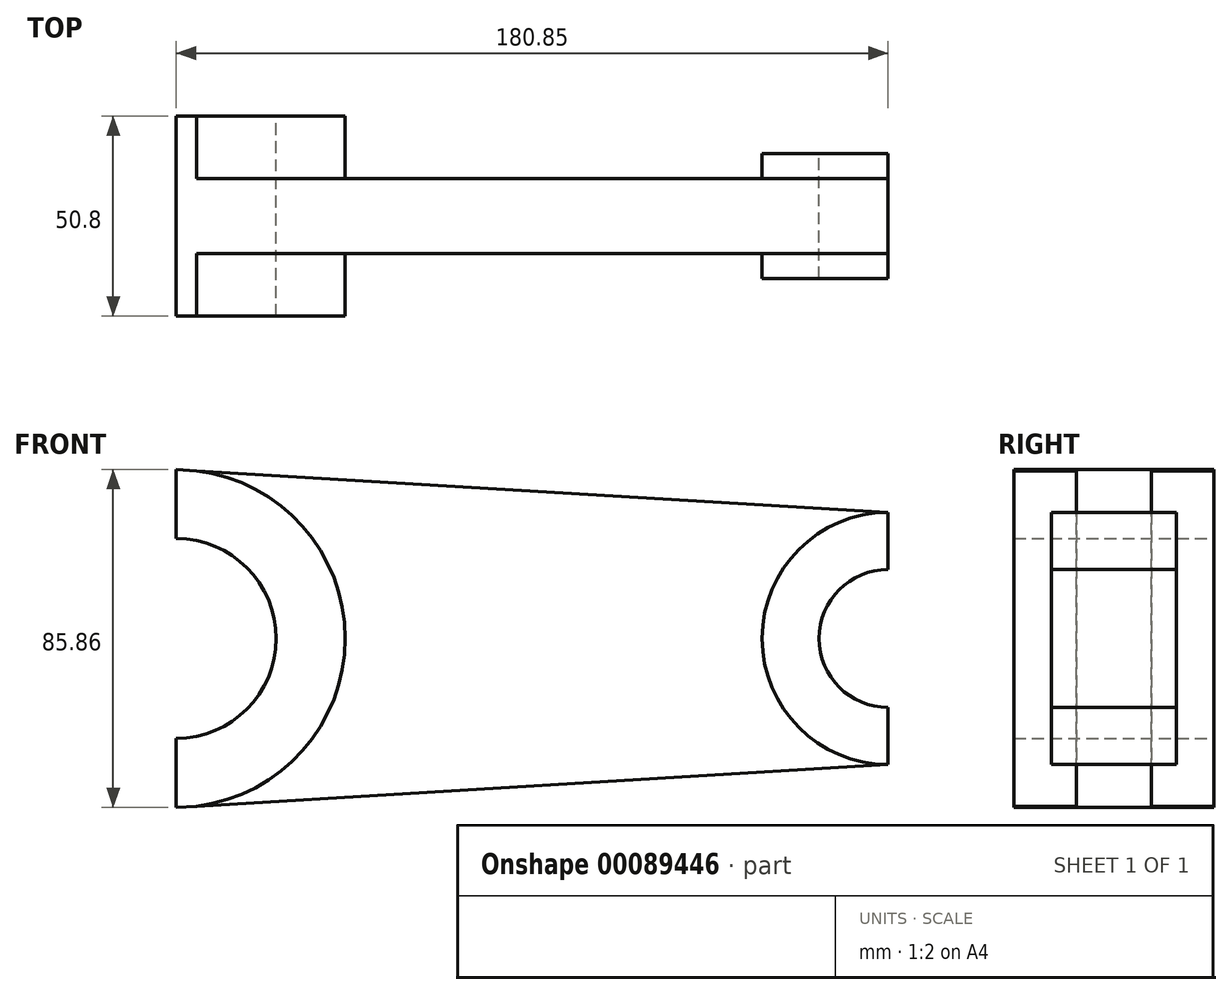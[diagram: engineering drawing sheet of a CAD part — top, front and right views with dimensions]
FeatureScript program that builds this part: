
annotation { "Feature Type Name" : "Feature", "Feature Type Description" : "" }
export const myFeature = defineFeature(function(context is Context, id is Id, definition is map)
    precondition{}
    {
        {
            var Q0;
            Q0=qCreatedBy(makeId("Front.planeOp"),FACE);
            var sketch = newSketch(context, id + "F0", { "sketchPlane" : qUnion([Q0])});
            skCircle(sketch, "E0", {"center": v(0, 0) * mm, "radius": 42.93 * mm});
            skLineSegment(sketch, "E1", {"start": v(0, 0) * mm, "end": v(180.85, 0) * mm});
            skCircle(sketch, "E2", {"center": v(180.85, 0) * mm, "radius": 32 * mm});
            skLineSegment(sketch, "E3", {"start": v(0, 0) * mm, "end": v(0, 42.93) * mm});
            skLineSegment(sketch, "E4", {"start": v(0, 42.93) * mm, "end": v(0, -42.93) * mm});
            skLineSegment(sketch, "E5", {"start": v(0, -42.93) * mm, "end": v(0, 0) * mm});
            skLineSegment(sketch, "E6", {"start": v(180.85, 0) * mm, "end": v(180.85, 32) * mm});
            skLineSegment(sketch, "E7", {"start": v(180.85, 32) * mm, "end": v(180.85, -32) * mm});
            skLineSegment(sketch, "E8", {"start": v(180.85, -32) * mm, "end": v(0, -42.93) * mm});
            skLineSegment(sketch, "E9", {"start": v(0, 42.93) * mm, "end": v(180.85, 32) * mm});
            skCircle(sketch, "E10", {"center": v(0, 0) * mm, "radius": 25.4 * mm});
            skCircle(sketch, "E11", {"center": v(180.85, 0) * mm, "radius": 17.53 * mm});
            skSolve(sketch);
        }
        {
            var Q0;
            {var subQ0=sQuery(id+"F0.wireOp",EDGE,"E8");var subQ1=sQuery(id+"F0.wireOp",EDGE,"E0");var subQ2=makeQuery(id+"F0.imprint","INTERSECT",VERTEX,{"derivedFrom":[subQ1,subQ0]});Q0=makeQuery(id+"F0.imprint","IMPRINT",FACE,{"disambiguationData":[TD([[makeQuery(id+"F0.imprint","IMPRINT",EDGE,{"disambiguationData":[TD([[subQ2,-1.0]])],"derivedFrom":subQ1}),-1.0]])]});}
            var Q1;
            {var subQ0=sQuery(id+"F0.wireOp",EDGE,"E9");var subQ1=sQuery(id+"F0.wireOp",EDGE,"E0");var subQ2=makeQuery(id+"F0.imprint","INTERSECT",VERTEX,{"derivedFrom":[subQ1,subQ0]});Q1=makeQuery(id+"F0.imprint","IMPRINT",FACE,{"disambiguationData":[TD([[makeQuery(id+"F0.imprint","IMPRINT",EDGE,{"disambiguationData":[TD([[subQ2,1.0]])],"derivedFrom":subQ1}),-1.0]])]});}
            extrude(context, id + "F1", {"entities" : qUnion([Q0, Q1]), "depth" : 19.05 * mm});
        }
        {
            var Q0;
            {var subQ0=sQuery(id+"F0.wireOp",EDGE,"E4");var subQ5=sQuery(id+"F0.wireOp",EDGE,"E10");var subQ6=makeQuery(id+"F0.imprint","INTERSECT",VERTEX,{"derivedFrom":[subQ0,subQ5]});Q0=makeQuery(id+"F0.imprint","IMPRINT",FACE,{"disambiguationData":[TD([[makeQuery(id+"F0.imprint","IMPRINT",EDGE,{"disambiguationData":[TD([[subQ6,-1.0]])],"derivedFrom":subQ5}),-1.0]])]});}
            var Q1;
            {var subQ0=sQuery(id+"F0.wireOp",EDGE,"E9");var subQ2=sQuery(id+"F0.wireOp",EDGE,"E0");var subQ9=makeQuery(id+"F0.imprint","INTERSECT",VERTEX,{"derivedFrom":[subQ2,subQ0]});Q1=makeQuery(id+"F0.imprint","IMPRINT",FACE,{"disambiguationData":[TD([[makeQuery(id+"F0.imprint","IMPRINT",EDGE,{"disambiguationData":[TD([[subQ9,1.0]])],"derivedFrom":subQ2}),1.0]])]});}
            var Q2;
            {var subQ0=sQuery(id+"F0.wireOp",EDGE,"E8");var subQ2=sQuery(id+"F0.wireOp",EDGE,"E0");var subQ6=makeQuery(id+"F0.imprint","INTERSECT",VERTEX,{"derivedFrom":[subQ2,subQ0]});Q2=makeQuery(id+"F0.imprint","IMPRINT",FACE,{"disambiguationData":[TD([[makeQuery(id+"F0.imprint","IMPRINT",EDGE,{"disambiguationData":[TD([[subQ6,-1.0]])],"derivedFrom":subQ2}),1.0]])]});}
            extrude(context, id + "F2", {"entities" : qUnion([Q0, Q1, Q2]), "operationType" : NewBodyOperationType.ADD, "depth" : 34.92 * mm});
        }
        {
            var Q0;
            {var subQ0=sQuery(id+"F0.wireOp",EDGE,"E2");var subQ1=sQuery(id+"F0.wireOp",EDGE,"E1");var subQ2=makeQuery(id+"F0.imprint","INTERSECT",VERTEX,{"derivedFrom":[subQ1,subQ0]});Q0=makeQuery(id+"F0.imprint","IMPRINT",FACE,{"disambiguationData":[TD([[makeQuery(id+"F0.imprint","IMPRINT",EDGE,{"disambiguationData":[TD([[subQ2,-1.0]])],"derivedFrom":subQ1}),1.0]])]});}
            var Q1;
            {var subQ0=sQuery(id+"F0.wireOp",EDGE,"E2");var subQ1=sQuery(id+"F0.wireOp",EDGE,"E1");var subQ2=makeQuery(id+"F0.imprint","INTERSECT",VERTEX,{"derivedFrom":[subQ1,subQ0]});Q1=makeQuery(id+"F0.imprint","IMPRINT",FACE,{"disambiguationData":[TD([[makeQuery(id+"F0.imprint","IMPRINT",EDGE,{"disambiguationData":[TD([[subQ2,-1.0]])],"derivedFrom":subQ1}),-1.0]])]});}
            var Q2;
            {var subQ0=sQuery(id+"F0.wireOp",EDGE,"E7");var subQ4=sQuery(id+"F0.wireOp",EDGE,"E11");var subQ5=makeQuery(id+"F0.imprint","INTERSECT",VERTEX,{"disambiguationData":[OD(0.0)],"derivedFrom":[subQ0,subQ4]});Q2=makeQuery(id+"F0.imprint","IMPRINT",FACE,{"disambiguationData":[TD([[makeQuery(id+"F0.imprint","IMPRINT",EDGE,{"disambiguationData":[TD([[subQ5,1.0]])],"derivedFrom":subQ4}),-1.0]])]});}
            var Q3;
            {var subQ0=sQuery(id+"F0.wireOp",EDGE,"E7");var subQ4=sQuery(id+"F0.wireOp",EDGE,"E11");var subQ5=makeQuery(id+"F0.imprint","INTERSECT",VERTEX,{"disambiguationData":[OD(0.0)],"derivedFrom":[subQ0,subQ4]});Q3=makeQuery(id+"F0.imprint","IMPRINT",FACE,{"disambiguationData":[TD([[makeQuery(id+"F0.imprint","IMPRINT",EDGE,{"disambiguationData":[TD([[subQ5,1.0]])],"derivedFrom":subQ4}),-1.0]])]});}
            extrude(context, id + "F3", {"entities" : qUnion([Q0, Q1, Q2, Q3]), "operationType" : NewBodyOperationType.ADD, "depth" : 25.4 * mm});
        }
        {
            var Q0;
            {var subQ0=sQuery(id+"F0.wireOp",EDGE,"E7");var subQ4=sQuery(id+"F0.wireOp",EDGE,"E11");var subQ5=makeQuery(id+"F0.imprint","INTERSECT",VERTEX,{"disambiguationData":[OD(0.0)],"derivedFrom":[subQ0,subQ4]});Q0=makeQuery(id+"F0.imprint","IMPRINT",FACE,{"disambiguationData":[TD([[makeQuery(id+"F0.imprint","IMPRINT",EDGE,{"disambiguationData":[TD([[subQ5,1.0]])],"derivedFrom":subQ4}),-1.0]])]});}
            var Q1;
            {var subQ0=sQuery(id+"F0.wireOp",EDGE,"E2");var subQ1=sQuery(id+"F0.wireOp",EDGE,"E1");var subQ2=makeQuery(id+"F0.imprint","INTERSECT",VERTEX,{"derivedFrom":[subQ1,subQ0]});Q1=makeQuery(id+"F0.imprint","IMPRINT",FACE,{"disambiguationData":[TD([[makeQuery(id+"F0.imprint","IMPRINT",EDGE,{"disambiguationData":[TD([[subQ2,-1.0]])],"derivedFrom":subQ1}),-1.0]])]});}
            var Q2;
            {var subQ0=sQuery(id+"F0.wireOp",EDGE,"E2");var subQ1=sQuery(id+"F0.wireOp",EDGE,"E1");var subQ2=makeQuery(id+"F0.imprint","INTERSECT",VERTEX,{"derivedFrom":[subQ1,subQ0]});Q2=makeQuery(id+"F0.imprint","IMPRINT",FACE,{"disambiguationData":[TD([[makeQuery(id+"F0.imprint","IMPRINT",EDGE,{"disambiguationData":[TD([[subQ2,-1.0]])],"derivedFrom":subQ1}),1.0]])]});}
            extrude(context, id + "F4", {"entities" : qUnion([Q0, Q1, Q2]), "operationType" : NewBodyOperationType.ADD, "oppositeDirection" : true, "depth" : 6.35 * mm});
        }
        {
            var Q0;
            {var subQ0=sQuery(id+"F0.wireOp",EDGE,"E9");var subQ2=sQuery(id+"F0.wireOp",EDGE,"E0");var subQ9=makeQuery(id+"F0.imprint","INTERSECT",VERTEX,{"derivedFrom":[subQ2,subQ0]});Q0=makeQuery(id+"F0.imprint","IMPRINT",FACE,{"disambiguationData":[TD([[makeQuery(id+"F0.imprint","IMPRINT",EDGE,{"disambiguationData":[TD([[subQ9,1.0]])],"derivedFrom":subQ2}),1.0]])]});}
            var Q1;
            {var subQ0=sQuery(id+"F0.wireOp",EDGE,"E4");var subQ5=sQuery(id+"F0.wireOp",EDGE,"E10");var subQ6=makeQuery(id+"F0.imprint","INTERSECT",VERTEX,{"derivedFrom":[subQ0,subQ5]});Q1=makeQuery(id+"F0.imprint","IMPRINT",FACE,{"disambiguationData":[TD([[makeQuery(id+"F0.imprint","IMPRINT",EDGE,{"disambiguationData":[TD([[subQ6,-1.0]])],"derivedFrom":subQ5}),-1.0]])]});}
            var Q2;
            {var subQ0=sQuery(id+"F0.wireOp",EDGE,"E8");var subQ2=sQuery(id+"F0.wireOp",EDGE,"E0");var subQ6=makeQuery(id+"F0.imprint","INTERSECT",VERTEX,{"derivedFrom":[subQ2,subQ0]});Q2=makeQuery(id+"F0.imprint","IMPRINT",FACE,{"disambiguationData":[TD([[makeQuery(id+"F0.imprint","IMPRINT",EDGE,{"disambiguationData":[TD([[subQ6,-1.0]])],"derivedFrom":subQ2}),1.0]])]});}
            extrude(context, id + "F5", {"entities" : qUnion([Q0, Q1, Q2]), "operationType" : NewBodyOperationType.ADD, "oppositeDirection" : true, "depth" : 15.88 * mm});
        }
    });
